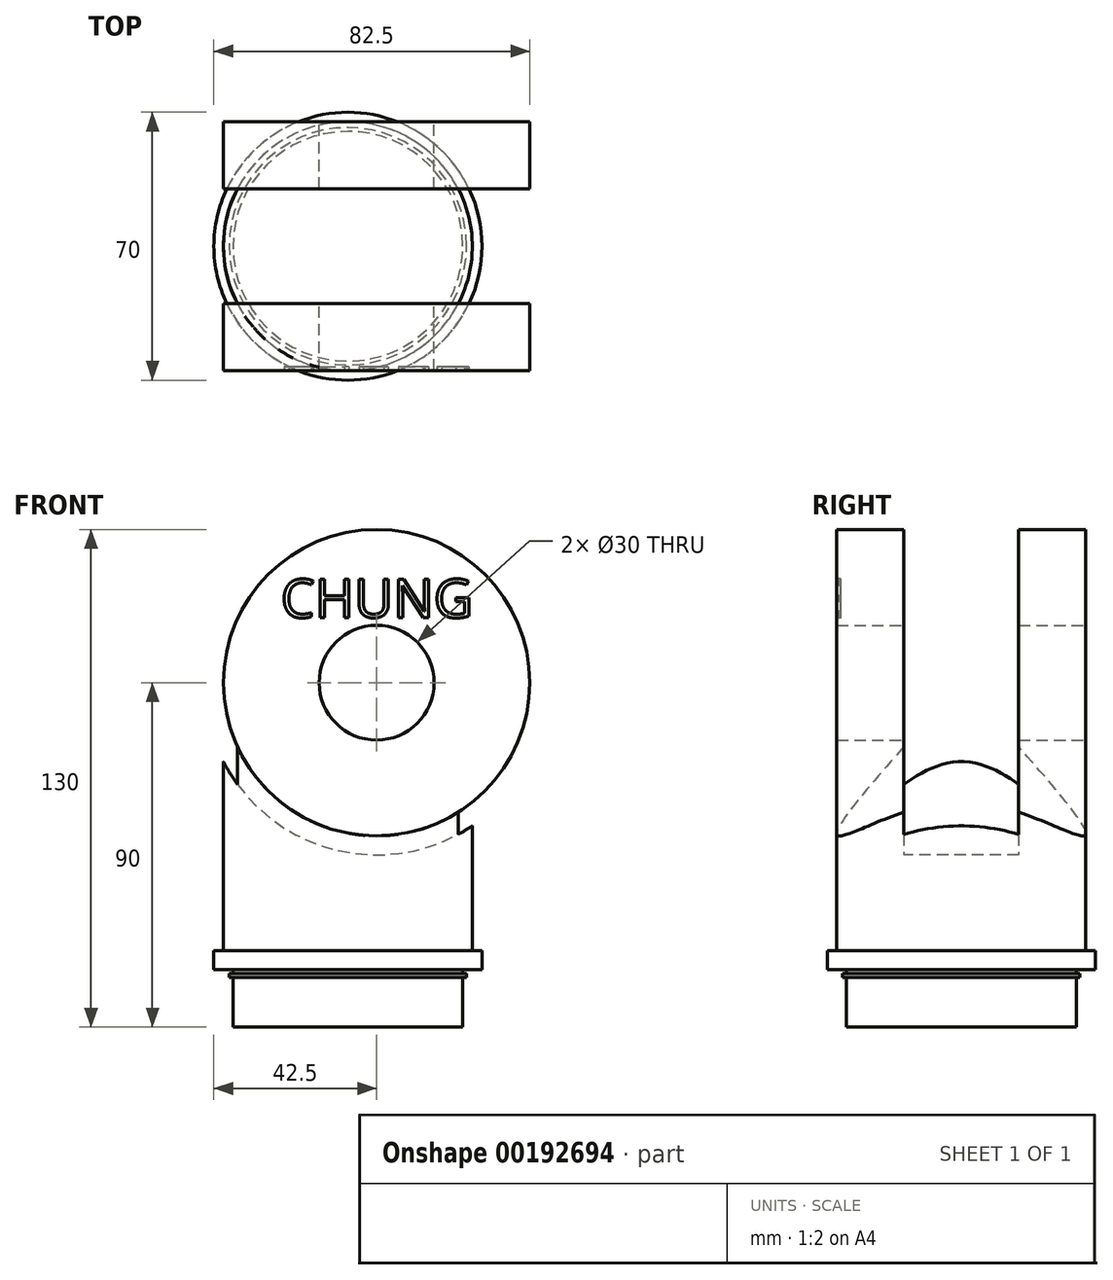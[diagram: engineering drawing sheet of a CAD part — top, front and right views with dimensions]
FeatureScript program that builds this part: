
annotation { "Feature Type Name" : "Feature", "Feature Type Description" : "" }
export const myFeature = defineFeature(function(context is Context, id is Id, definition is map)
    precondition{}
    {
        {
            var Q0;
            Q0=qCreatedBy(makeId("Front.planeOp"),FACE);
            var sketch = newSketch(context, id + "F0", { "sketchPlane" : qUnion([Q0])});
            skLineSegment(sketch, "E0", {"start": v(0, 0) * mm, "end": v(0, 20) * mm});
            skLineSegment(sketch, "E1", {"start": v(0, 20) * mm, "end": v(-35, 20) * mm});
            skLineSegment(sketch, "E2", {"start": v(-35, 20) * mm, "end": v(-35, 15) * mm});
            skLineSegment(sketch, "E3", {"start": v(-35, 15) * mm, "end": v(-30, 15) * mm});
            skLineSegment(sketch, "E4", {"start": v(-30, 15) * mm, "end": v(-30, 14) * mm});
            skLineSegment(sketch, "E5", {"start": v(-30, 14) * mm, "end": v(-31, 14) * mm});
            skLineSegment(sketch, "E6", {"start": v(-31, 14) * mm, "end": v(-31, 13) * mm});
            skLineSegment(sketch, "E7", {"start": v(-31, 13) * mm, "end": v(-30, 13) * mm});
            skLineSegment(sketch, "E8", {"start": v(-30, 13) * mm, "end": v(-30, 0) * mm});
            skLineSegment(sketch, "E9", {"start": v(-30, 0) * mm, "end": v(0, 0) * mm});
            skSolve(sketch);
        }
        {
            var Q0;
            Q0 = qSketchRegion(id + "F0", true);
            var Q1;
            Q1=sQuery(id+"F0.wireOp",EDGE,"E0");
            revolve(context, id + "F1", {"entities" : qUnion([Q0]), "axis" : qUnion([Q1]), "revolveType" : RevolveType.FULL});
        }
        {
            var Q0;
            Q0=makeQuery(id+"F1.opRevolve","SWEPT_FACE",FACE,{"disambiguationData":[OSD([sQuery(id+"F0.wireOp",EDGE,"E1")])]});
            var sketch = newSketch(context, id + "F2", { "sketchPlane" : qUnion([Q0])});
            skCircle(sketch, "E10", {"center": v(0, 0) * mm, "radius": 32.5 * mm});
            skSolve(sketch);
        }
        {
            var Q0;
            Q0 = qSketchRegion(id + "F2", true);
            var Q1;
            Q1 = qSketchRegion(id + "F6", true);
            extrude(context, id + "F3", {"entities" : qUnion([Q0, Q1]), "operationType" : NewBodyOperationType.ADD, "depth" : 70 * mm});
        }
        {
            var Q0;
            Q0=qCreatedBy(makeId("Front.planeOp"),FACE);
            var sketch = newSketch(context, id + "F4", { "sketchPlane" : qUnion([Q0])});
            skCircle(sketch, "E11", {"center": v(7.5, 90) * mm, "radius": 40 * mm});
            skSolve(sketch);
        }
        {
            var Q0;
            Q0 = qSketchRegion(id + "F4", true);
            extrude(context, id + "F5", {"entities" : qUnion([Q0]), "operationType" : NewBodyOperationType.ADD, "endBound" : BoundingType.SYMMETRIC, "depth" : 65 * mm});
        }
        {
            var Q0;
            Q0=qCreatedBy(makeId("Front.planeOp"),FACE);
            var sketch = newSketch(context, id + "F6", { "sketchPlane" : qUnion([Q0])});
            skSolve(sketch);
        }
        {
            var Q0;
            Q0=qCreatedBy(makeId("Front.planeOp"),FACE);
            var sketch = newSketch(context, id + "F7", { "sketchPlane" : qUnion([Q0])});
            skCircle(sketch, "E12", {"center": v(7.5, 90) * mm, "radius": 45 * mm});
            skSolve(sketch);
        }
        {
            var Q0;
            Q0 = qSketchRegion(id + "F7", true);
            extrude(context, id + "F8", {"entities" : qUnion([Q0]), "operationType" : NewBodyOperationType.REMOVE, "endBound" : BoundingType.SYMMETRIC, "oppositeDirection" : true, "depth" : 30 * mm});
        }
        {
            var Q0;
            Q0=makeQuery(id+"F5.opExtrude","CAP_FACE",FACE,{"disambiguationData":[OSD([sQuery(id+"F4.wireOp",EDGE,"E11")])],"isStart":true});
            var sketch = newSketch(context, id + "F9", { "sketchPlane" : qUnion([Q0])});
            skCircle(sketch, "E13", {"center": v(-7.5, 90) * mm, "radius": 15 * mm});
            skSolve(sketch);
        }
        {
            var Q0;
            Q0 = qSketchRegion(id + "F9", true);
            extrude(context, id + "F10", {"entities" : qUnion([Q0]), "operationType" : NewBodyOperationType.REMOVE, "endBound" : BoundingType.THROUGH_ALL, "oppositeDirection" : true, "depth" : 25 * mm});
        }
        {
            var Q0;
            Q0=makeQuery(id+"F5.opExtrude","CAP_FACE",FACE,{"disambiguationData":[OSD([sQuery(id+"F4.wireOp",EDGE,"E11")])],"isStart":false});
            var sketch = newSketch(context, id + "F11", { "sketchPlane" : qUnion([Q0])});
            skText(sketch, "E14", { "text": "CHUNG", "fontName": "OpenSans-Regular.ttf"});
            const initialGuessF11  = {"E14": [-0.0175, 0.107, 1, 0, 0.01008]};
            skSetInitialGuess(sketch, initialGuessF11);
            skSolve(sketch);
        }
        {
            var Q0;
            Q0 = qSketchRegion(id + "F11", true);
            extrude(context, id + "F12", {"entities" : qUnion([Q0]), "operationType" : NewBodyOperationType.REMOVE, "oppositeDirection" : true, "depth" : 1 * mm});
        }
    });
